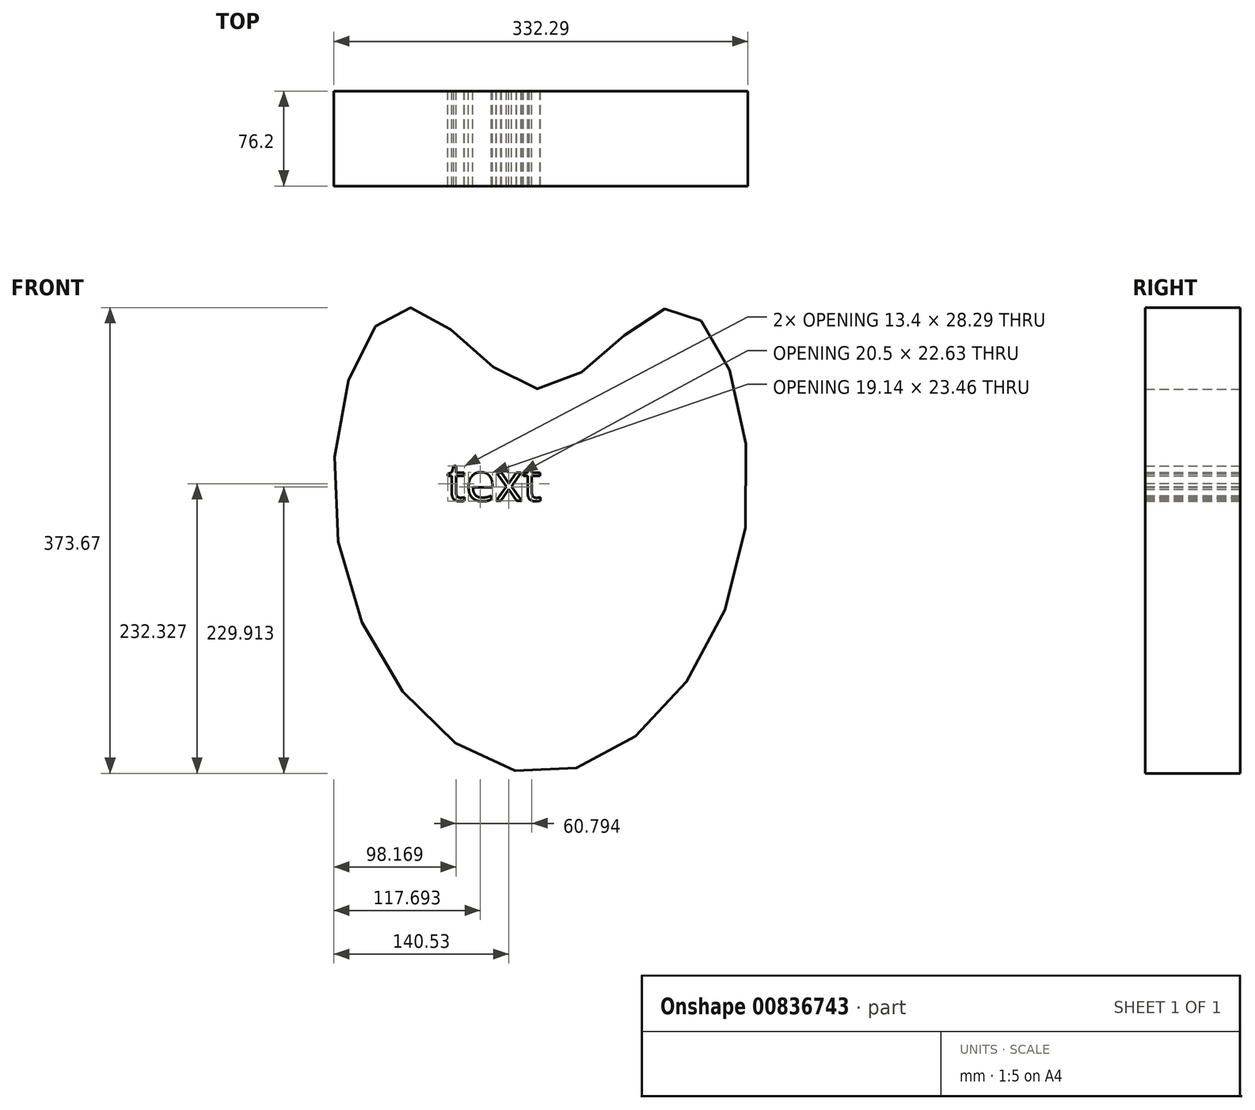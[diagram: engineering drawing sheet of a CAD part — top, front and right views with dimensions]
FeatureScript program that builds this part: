
annotation { "Feature Type Name" : "Feature", "Feature Type Description" : "" }
export const myFeature = defineFeature(function(context is Context, id is Id, definition is map)
    precondition{}
    {
        {
            var Q0;
            Q0=qCreatedBy(makeId("Front.planeOp"),FACE);
            var sketch = newSketch(context, id + "F0", { "sketchPlane" : qUnion([Q0])});
            skFitSpline(sketch, "E0", {"points": [v(-294.4, -122.47) * mm, v(-238.1, 65.36) * mm, v(-131.84, 0) * mm, v(-25.59, 65.36) * mm, v(30.72, -122.47) * mm, v(-131.84, -308.3) * mm, v(-294.4, -122.47) * mm]});
            skLineSegment(sketch, "E1", {"start": v(-131.84, 49.52) * mm, "end": v(-131.84, -331.65) * mm, "construction": true});
            skText(sketch, "E2", { "text": "text", "fontName": "OpenSans-Regular.ttf"});
            const initialGuessF0  = {"E2": [-0.20716, -0.0897, 1, 0, 0.03044]};
            skSetInitialGuess(sketch, initialGuessF0);
            skSolve(sketch);
        }
        {
            var Q0;
            Q0 = qSketchRegion(id + "F0", true);
            extrude(context, id + "F1", {"entities" : qUnion([Q0]), "depth" : 76.2 * mm, "offsetDistance" : 25.4 * mm});
        }
    });
